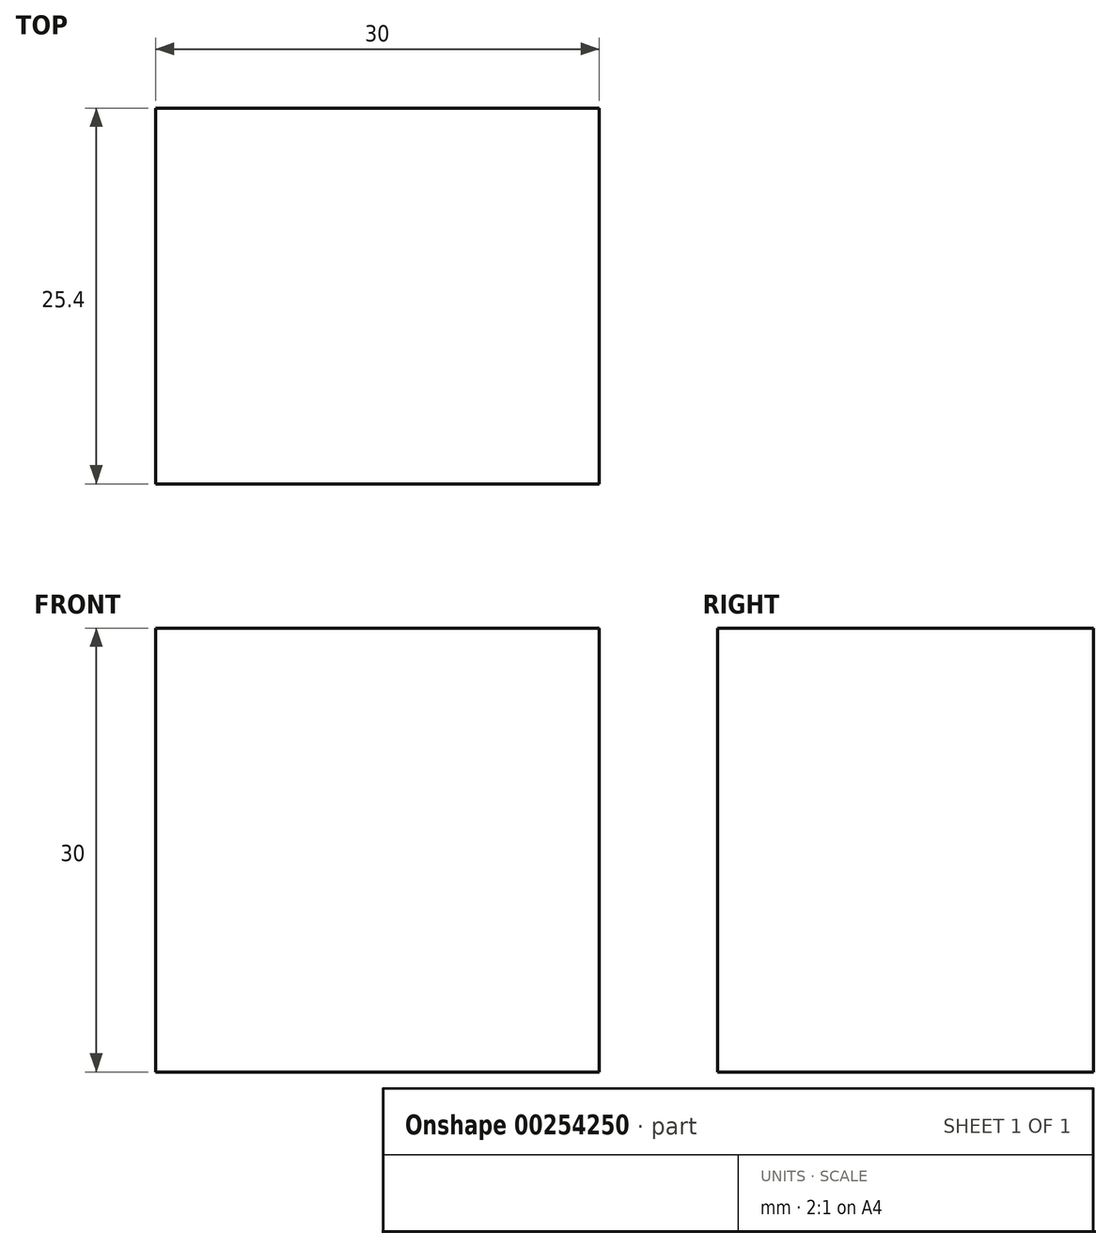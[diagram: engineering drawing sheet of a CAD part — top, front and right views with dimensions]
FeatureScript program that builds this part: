
annotation { "Feature Type Name" : "Feature", "Feature Type Description" : "" }
export const myFeature = defineFeature(function(context is Context, id is Id, definition is map)
    precondition{}
    {
        {
            var Q0;
            Q0=qCreatedBy(makeId("Front.planeOp"),FACE);
            var sketch = newSketch(context, id + "F0", { "sketchPlane" : qUnion([Q0])});
            skLineSegment(sketch, "E0.bottom", {"start": v(0, 0) * mm, "end": v(-30, 0) * mm});
            skLineSegment(sketch, "E0.top", {"start": v(0, 30) * mm, "end": v(-30, 30) * mm});
            skLineSegment(sketch, "E0.left", {"start": v(0, 0) * mm, "end": v(0, 30) * mm});
            skLineSegment(sketch, "E0.right", {"start": v(-30, 0) * mm, "end": v(-30, 30) * mm});
            skSolve(sketch);
        }
        {
            var Q0;
            Q0=makeQuery(id+"F0.imprint","IMPRINT",FACE,{"disambiguationData":[TD([[makeQuery(id+"F0.imprint","IMPRINT",EDGE,{"derivedFrom":sQuery(id+"F0.wireOp",EDGE,"E0.bottom")}),-1.0]])]});
            extrude(context, id + "F1", {"entities" : qUnion([Q0]), "depth" : 25.4 * mm});
        }
    });
